# Revit family: KEUCO_53920010100
name_source: partatom
category: Sanitärinstallationen
revit_build: Autodesk Revit 2016 (Build: 20150220_1215(x64)
units: mm (PartAtom-declared; Revit-internal decimal feet)

## family parameters
Arbeitsebenenbasiert = Nein
Beim Laden mit Abzugskörper schneiden = Nein
Bemaßung runder Anschluss = Durchmesser verwenden
Gemeinsam genutzt = Nein
Immer vertikal = Ja
OmniClass-Nummer = 23.45.00.00
Raumberechnungspunkt = Nein
Teiletyp = Normal

## types (3) — shared parameters
Gewicht = 4.292
Hersteller = KEUCO
Kategorie = ARM
Preisgruppe = 1
Serie = Plan S
URL = https://www.keuco.com
VerbindungsAbstand = 150 mm
Verwendung = WA

## per-type parameters (varying)
| type | Ausschreibungstext | Beschreibung | Länge |
| 53920010100 | KEUCO PLAN BLUE Wannenmischer DN15, 53920010100
hochglanzverchromter Wannenmischer, DN15, 
in ästhetischem, funktionalem Design, 
für Aufputz Montage, 
Mischventil mit keramischen Dichtscheiben, 
Ab- und Umstellventil mit keramischen Dichtscheiben,
Betätigungselement aus Metall,
Schlauchanschluss DN 15,
Durchflussmenge begrenzt auf 12 l/min.,
Eigensicherung gegen Rückfließen,
M 28x1 Luftsprudler, Durchflussmenge ca. 24 l/min.,
geeignet für Durchlauferhitzer,
Grundkörperdurchmesser 44 mm, Breite 310 mm,
Ausladung 222 mm
Rosettenkappe, Durchmesser 69 mm, 
als Design-Element ebenfalls hochglanzverchromt,
Stichmaß 150 mm, Toleranzklasse +/- 14 mm | für AP Montage
Ab- und Umstellventil mit keramischen Dichtscheiben,
Mischventil mit keramischen Dichtscheiben,
Schlauchanschluss DN15
(Durchflussmenge begrenzt auf 12 l/min.),
Eigensicher gegen Rückfließen,
Stichmaß 150 +/- 14 mm,
für Durchlauferhitzer geeignet,
mit Luftsprudler M 28x1,
Durchflussmenge ca. 24 l/min.
geräuschgeprüft | 222 mm |
| 52920070100 | KEUCO PLAN S - Wannenmischer DN 15, 52920070100
Wannenmischer in Edelstahl-finish, DN 15,
in ästhetischem Design,für Aufputz-Montage, 
Ab- und Umstellventil mit keramischen Dichtscheiben,
Mischventil mit keramischen Dichtscheiben,
Schlauchanschluss DN 15, Durchflussmenge begrenzt auf 15 l/min.,
Eigensicher gegen Rückfließen,
Luftsprudler M24 x 1, Durchflussmenge ca. 35 l/min.,
geeignet für Durchlauferhitzer,
Gesamthöhe 124 mm, Breite 350 mm, Ausladung max. 218 mm,
Stichmaß 150 mm, Toleranzklasse +/- 14 mm | für AP Montage
Ab- und Umstellventil mit keramischen Dichtscheiben,
Mischventil mit keramischen Dichtscheiben,
Schlauchanschluss DN15
(Durchflussmenge begrenzt auf 15 l/min.),
Eigensicher gegen Rückfließen,
Stichmaß 150 +/- 14 mm,
für Durchlauferhitzer geeignet,
mit Luftsprudler M 28x1,
Durchflussmenge ca. 35 l/min. | 170 mm |
| 52920170100 | KEUCO PLAN S - Wannenmischer DN 15, 52920170100
Wannenmischer in Aluminium-finish, DN 15,
in ästhetischem Design,für Aufputz-Montage, 
Ab- und Umstellventil mit keramischen Dichtscheiben,
Mischventil mit keramischen Dichtscheiben,
Schlauchanschluss DN 15, Durchflussmenge begrenzt auf 15 l/min.,
Eigensicher gegen Rückfließen,
Luftsprudler M24 x 1, Durchflussmenge ca. 35 l/min.,
geeignet für Durchlauferhitzer,
Gesamthöhe 124 mm, Breite 350 mm, Ausladung max. 218 mm,
Stichmaß 150 mm, Toleranzklasse +/- 14 mm | für AP Montage
Ab- und Umstellventil mit keramischen Dichtscheiben,
Mischventil mit keramischen Dichtscheiben,
Schlauchanschluss DN15
(Durchflussmenge begrenzt auf 15 l/min.),
Eigensicher gegen Rückfließen,
Stichmaß 150 +/- 14 mm,
für Durchlauferhitzer geeignet,
mit Luftsprudler M 28x1,
Durchflussmenge ca. 35 l/min. | 170 mm |

note: column(s) folded — value = type name in every type: Artikelnummer

## geometry (parser evidence)
native form markers: Blend x2, Sweep x3
no freeform markers — native parametric forms only
